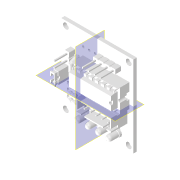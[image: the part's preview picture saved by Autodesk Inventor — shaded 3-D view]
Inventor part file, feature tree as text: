
AUTODESK INVENTOR PART (.ipt)
format: ipt  version: 2022 (Build 260153000, 153)  size: 4,866,560 bytes
history: native  units: mm
features: other x67, plane x2
ambient origin geometry x8: Origin, YZ Plane, XZ Plane, XY Plane, X Axis, Y Axis, Z Axis, Center Point
bodies: Volumenkörper1 (feature_tree), Volumenkörper2 (feature_tree), Volumenkörper3 (feature_tree), Volumenkörper4 (feature_tree), Volumenkörper5 (feature_tree), Volumenkörper6 (feature_tree), Volumenkörper7 (feature_tree), Volumenkörper8 (feature_tree), Volumenkörper9 (feature_tree), Volumenkörper10 (feature_tree), Volumenkörper11 (feature_tree), Volumenkörper12 (feature_tree), Volumenkörper13 (feature_tree), Volumenkörper14 (feature_tree), Volumenkörper15 (feature_tree), Volumenkörper16 (feature_tree), Volumenkörper17 (feature_tree), Volumenkörper18 (feature_tree), Volumenkörper19 (feature_tree), Volumenkörper20 (feature_tree), Volumenkörper21 (feature_tree), Volumenkörper22 (feature_tree), Volumenkörper23 (feature_tree), Volumenkörper24 (feature_tree), Volumenkörper25 (feature_tree), Volumenkörper26 (feature_tree), Volumenkörper27 (feature_tree), Volumenkörper28 (feature_tree), Volumenkörper29 (feature_tree), Volumenkörper30 (feature_tree), Volumenkörper31 (feature_tree), Volumenkörper32 (feature_tree), Volumenkörper33 (feature_tree), Volumenkörper34 (feature_tree), Volumenkörper35 (feature_tree), Volumenkörper36 (feature_tree), Volumenkörper37 (feature_tree), Volumenkörper38 (feature_tree), Volumenkörper39 (feature_tree), Volumenkörper40 (feature_tree), Volumenkörper41 (feature_tree), Volumenkörper42 (feature_tree), Volumenkörper43 (feature_tree), Volumenkörper44 (feature_tree), Volumenkörper45 (feature_tree), Volumenkörper46 (feature_tree), Volumenkörper47 (feature_tree), Volumenkörper48 (feature_tree), Volumenkörper49 (feature_tree), Volumenkörper50 (feature_tree), Volumenkörper51 (feature_tree), Volumenkörper52 (feature_tree), Volumenkörper53 (feature_tree), Volumenkörper54 (feature_tree), Volumenkörper55 (feature_tree), Volumenkörper56 (feature_tree), Volumenkörper57 (feature_tree), Volumenkörper58 (feature_tree), Volumenkörper59 (feature_tree), Volumenkörper60 (feature_tree), Volumenkörper61 (feature_tree), Volumenkörper62 (feature_tree), Volumenkörper63 (feature_tree), Volumenkörper64 (feature_tree), Volumenkörper65 (feature_tree), Volumenkörper66 (feature_tree), Volumenkörper67 (feature_tree)
feature tree (69):
  plane  "Arbeitsebene1"
  plane  "Arbeitsebene2"
  other  "brep_1"
  other  "brep_2"
  other  "brep_3"
  other  "brep_4"
  other  "brep_5"
  other  "brep_6"
  other  "brep_7"
  other  "brep_8"
  other  "brep_9"
  other  "brep_10"
  other  "brep_11"
  other  "brep_12"
  other  "brep_13"
  other  "brep_14"
  other  "brep_15"
  other  "brep_16"
  other  "brep_17"
  other  "brep_18"
  other  "brep_19"
  other  "brep_20"
  other  "brep_21"
  other  "brep_22"
  other  "brep_23"
  other  "brep_24"
  other  "brep_25"
  other  "brep_26"
  other  "brep_27"
  other  "brep_28"
  other  "brep_29"
  other  "brep_30"
  other  "brep_31"
  other  "brep_32"
  other  "brep_33"
  other  "brep_34"
  other  "brep_35"
  other  "brep_36"
  other  "brep_37"
  other  "brep_38"
  other  "brep_39"
  other  "brep_40"
  other  "brep_41"
  other  "brep_42"
  other  "brep_43"
  other  "brep_44"
  other  "brep_45"
  other  "brep_46"
  other  "brep_47"
  other  "brep_48"
  other  "brep_49"
  other  "brep_50"
  other  "brep_51"
  other  "brep_52"
  other  "brep_53"
  other  "brep_54"
  other  "brep_55"
  other  "brep_56"
  other  "brep_57"
  other  "brep_58"
  other  "brep_59"
  other  "brep_60"
  other  "brep_61"
  other  "brep_62"
  other  "brep_63"
  other  "brep_64"
  other  "brep_65"
  other  "brep_66"
  other  "brep_67"
